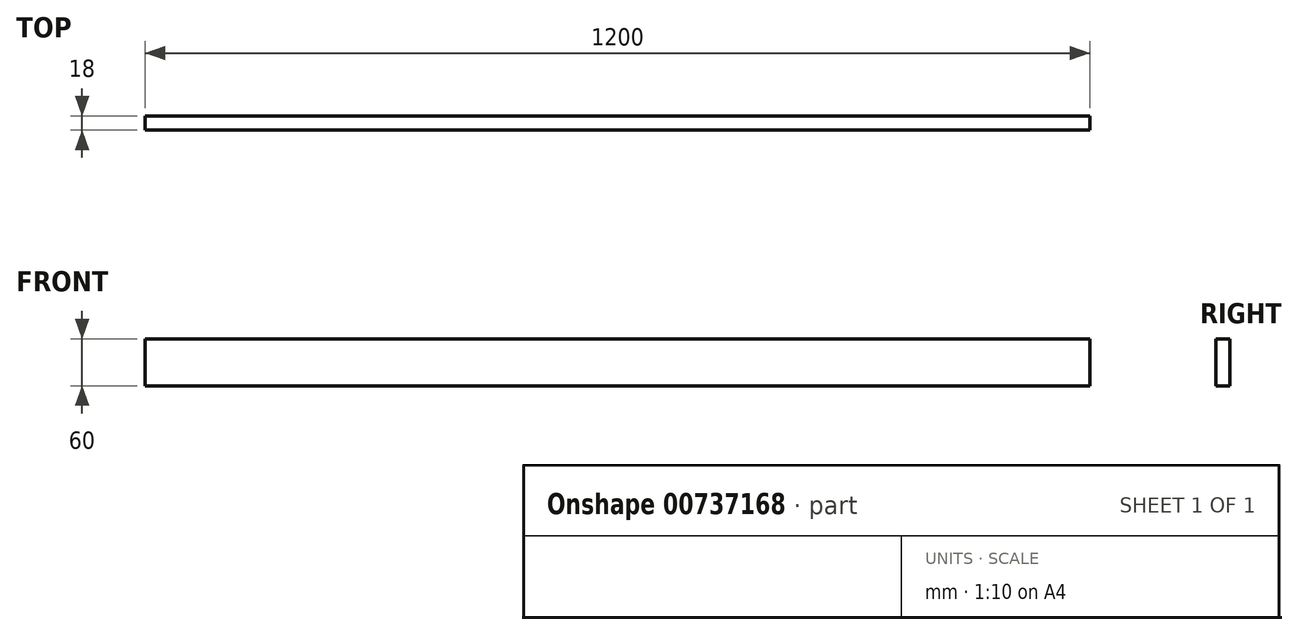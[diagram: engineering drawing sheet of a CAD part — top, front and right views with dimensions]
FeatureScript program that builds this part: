
annotation { "Feature Type Name" : "Feature", "Feature Type Description" : "" }
export const myFeature = defineFeature(function(context is Context, id is Id, definition is map)
    precondition{}
    {
        {
            var Q0;
            Q0=qCreatedBy(makeId("Front.planeOp"),FACE);
            var sketch = newSketch(context, id + "F0", { "sketchPlane" : qUnion([Q0])});
            skLineSegment(sketch, "E0.bottom", {"start": v(600, 30) * mm, "end": v(-600, 30) * mm});
            skLineSegment(sketch, "E0.top", {"start": v(600, -30) * mm, "end": v(-600, -30) * mm});
            skLineSegment(sketch, "E0.left", {"start": v(600, 30) * mm, "end": v(600, -30) * mm});
            skLineSegment(sketch, "E0.right", {"start": v(-600, 30) * mm, "end": v(-600, -30) * mm});
            skPoint(sketch, "E0.middle", {"position": v(0, 0) * mm});
            skSolve(sketch);
        }
        {
            var Q0;
            Q0 = qSketchRegion(id + "F0", true);
            extrude(context, id + "F1", {"entities" : qUnion([Q0]), "depth" : 18 * mm, "offsetDistance" : 25 * mm});
        }
    });
